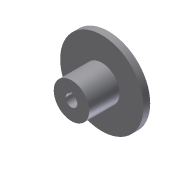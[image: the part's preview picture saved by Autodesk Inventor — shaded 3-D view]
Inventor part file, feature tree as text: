
AUTODESK INVENTOR PART (.ipt)
format: ipt  version: 2011 (Build 150239000, 239)  size: 92,672 bytes
history: native  units: in
note: dims shown in document units (in); Inventor stores cm internally (conversion verified against a paired STEP export)
features: extrude x3, sketch x3
ambient origin geometry x8: Origin, YZ Plane, XZ Plane, XY Plane, X Axis, Y Axis, Z Axis, Center Point
bodies: Solid1 (feature_tree)
feature tree (6):
  extrude  "Extrusion1"  Depth=0.18in TaperAngle=0.0deg
  extrude  "Extrusion2"  Depth=0.82in TaperAngle=0.0deg
  extrude  "Extrusion3"  Depth=0.0787in
  sketch  "Sketch1"  dims[d0=2.25in d1=0.18in d2=0.0in]
  sketch  "Sketch2"  dims[d3=0.958in d4=0.82in d5=0.0in]
  sketch  "Sketch3"  dims[d6=0.315in d7=0.0787in d8=0.0787in d9=0.82in d10=0.0in]
